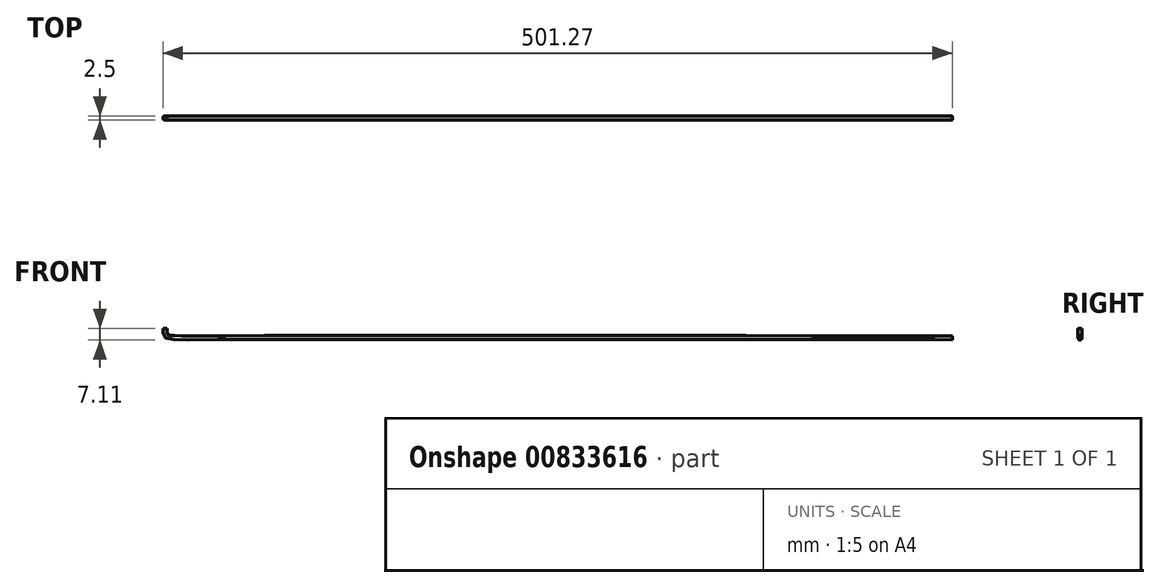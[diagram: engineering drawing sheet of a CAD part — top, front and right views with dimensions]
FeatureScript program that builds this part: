
annotation { "Feature Type Name" : "Feature", "Feature Type Description" : "" }
export const myFeature = defineFeature(function(context is Context, id is Id, definition is map)
    precondition{}
    {
        {
            var Q0;
            Q0=qCreatedBy(makeId("Top.planeOp"),FACE);
            var sketch = newSketch(context, id + "F0", { "sketchPlane" : qUnion([Q0])});
            skCircle(sketch, "E0", {"center": v(0, 0) * mm, "radius": 1.25 * mm});
            skSolve(sketch);
        }
        {
            var Q0;
            Q0=qCreatedBy(makeId("Front.planeOp"),FACE);
            var sketch = newSketch(context, id + "F1", { "sketchPlane" : qUnion([Q0])});
            skFitSpline(sketch, "E1", {"points": [v(-1.25, 0) * mm, v(-1.25, -1.2) * mm, v(-1.25, -2.02) * mm, v(-1.25, -3.17) * mm, v(-0.54, -5) * mm, v(2.12, -6.57) * mm, v(7.82, -6.99) * mm, v(15.3, -7.1) * mm, v(28.07, -7.05) * mm, v(500, -7.05) * mm], "startDerivative": vector(-0.09, -19.63) * mm, "endDerivative": vector(26.93, -0.1) * mm});
            skSolve(sketch);
        }
        {
            var Q0;
            Q0=makeQuery(id+"F0.imprint","IMPRINT",FACE,{"disambiguationData":[TD([[makeQuery(id+"F0.imprint","IMPRINT",EDGE,{"derivedFrom":sQuery(id+"F0.wireOp",EDGE,"E0")}),1.0]])]});
            var Q1;
            Q1=sQuery(id+"F1.wireOp",EDGE,"E1");
            sweep(context, id + "F2", {"profiles" : qUnion([Q0]), "path" : qUnion([Q1])});
        }
    });
